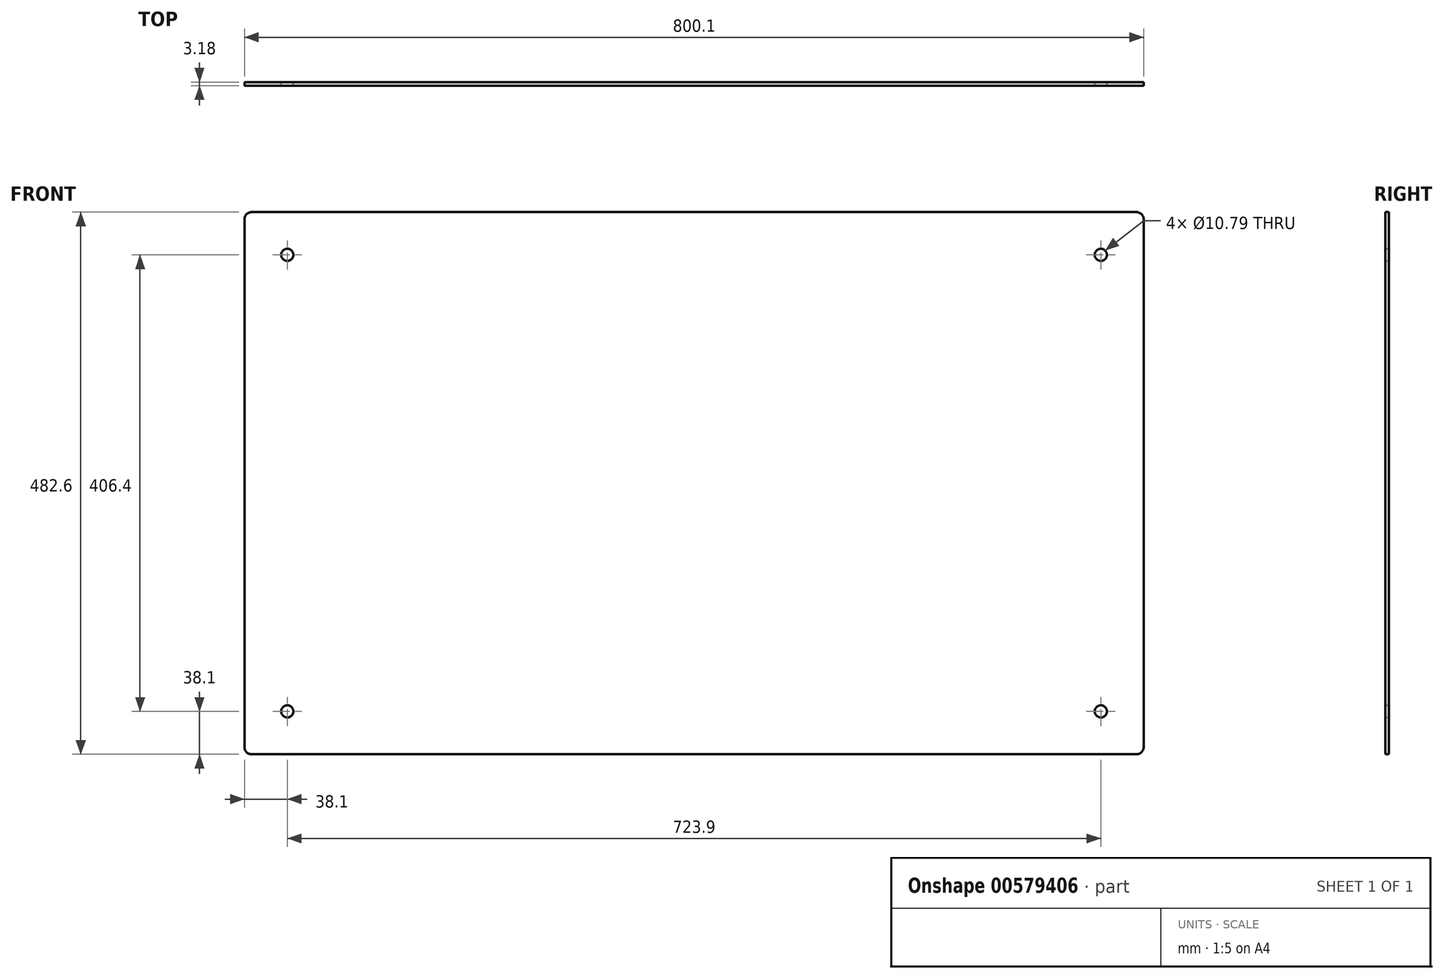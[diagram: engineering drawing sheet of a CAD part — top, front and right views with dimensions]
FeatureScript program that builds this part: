
annotation { "Feature Type Name" : "Feature", "Feature Type Description" : "" }
export const myFeature = defineFeature(function(context is Context, id is Id, definition is map)
    precondition{}
    {
        {
            var Q0;
            Q0=qCreatedBy(makeId("Front.planeOp"),FACE);
            var sketch = newSketch(context, id + "F0", { "sketchPlane" : qUnion([Q0])});
            skLineSegment(sketch, "E0.bottom", {"start": v(393.7, -241.3) * mm, "end": v(-393.7, -241.3) * mm});
            skLineSegment(sketch, "E0.top", {"start": v(393.7, 241.3) * mm, "end": v(-393.7, 241.3) * mm});
            skLineSegment(sketch, "E0.left", {"start": v(400.05, -234.95) * mm, "end": v(400.05, 234.95) * mm});
            skLineSegment(sketch, "E0.right", {"start": v(-400.05, -234.95) * mm, "end": v(-400.05, 234.95) * mm});
            skPoint(sketch, "E0.middle", {"position": v(0, 0) * mm});
            skLineSegment(sketch, "E1.bottom", {"start": v(361.95, -203.2) * mm, "end": v(-361.95, -203.2) * mm, "construction": true});
            skLineSegment(sketch, "E1.top", {"start": v(361.95, 203.2) * mm, "end": v(-361.95, 203.2) * mm, "construction": true});
            skLineSegment(sketch, "E1.left", {"start": v(361.95, -203.2) * mm, "end": v(361.95, 203.2) * mm, "construction": true});
            skLineSegment(sketch, "E1.right", {"start": v(-361.95, -203.2) * mm, "end": v(-361.95, 203.2) * mm, "construction": true});
            skCircle(sketch, "E2", {"center": v(-361.95, 203.2) * mm, "radius": 5.4 * mm});
            skCircle(sketch, "E3", {"center": v(361.95, 203.2) * mm, "radius": 5.4 * mm});
            skCircle(sketch, "E4", {"center": v(361.95, -203.2) * mm, "radius": 5.4 * mm});
            skCircle(sketch, "E5", {"center": v(-361.95, -203.2) * mm, "radius": 5.4 * mm});
            skPoint(sketch, "E6.visualSharp", {"position": v(-400.05, 241.3) * mm});
            skArc(sketch, "E6.filletArc", {"start": v(-393.7, 241.3) * mm, "mid": v(-398.2, 239.44) * mm, "end": v(-400.05, 234.95) * mm});
            skPoint(sketch, "E7.visualSharp", {"position": v(400.05, 241.3) * mm});
            skArc(sketch, "E7.filletArc", {"start": v(400.05, 234.95) * mm, "mid": v(398.2, 239.44) * mm, "end": v(393.7, 241.3) * mm});
            skPoint(sketch, "E8.visualSharp", {"position": v(400.05, -241.3) * mm});
            skArc(sketch, "E8.filletArc", {"start": v(393.7, -241.3) * mm, "mid": v(398.2, -239.44) * mm, "end": v(400.05, -234.95) * mm});
            skPoint(sketch, "E9.visualSharp", {"position": v(-400.05, -241.3) * mm});
            skArc(sketch, "E9.filletArc", {"start": v(-400.05, -234.95) * mm, "mid": v(-398.2, -239.44) * mm, "end": v(-393.7, -241.3) * mm});
            skSolve(sketch);
        }
        {
            var Q0;
            Q0=makeQuery(id+"F0.imprint","IMPRINT",FACE,{"disambiguationData":[TD([[makeQuery(id+"F0.imprint","IMPRINT",EDGE,{"derivedFrom":sQuery(id+"F0.wireOp",EDGE,"E0.bottom")}),-1.0]])]});
            extrude(context, id + "F1", {"entities" : qUnion([Q0]), "depth" : 3.17 * mm, "offsetDistance" : 25.4 * mm});
        }
    });
